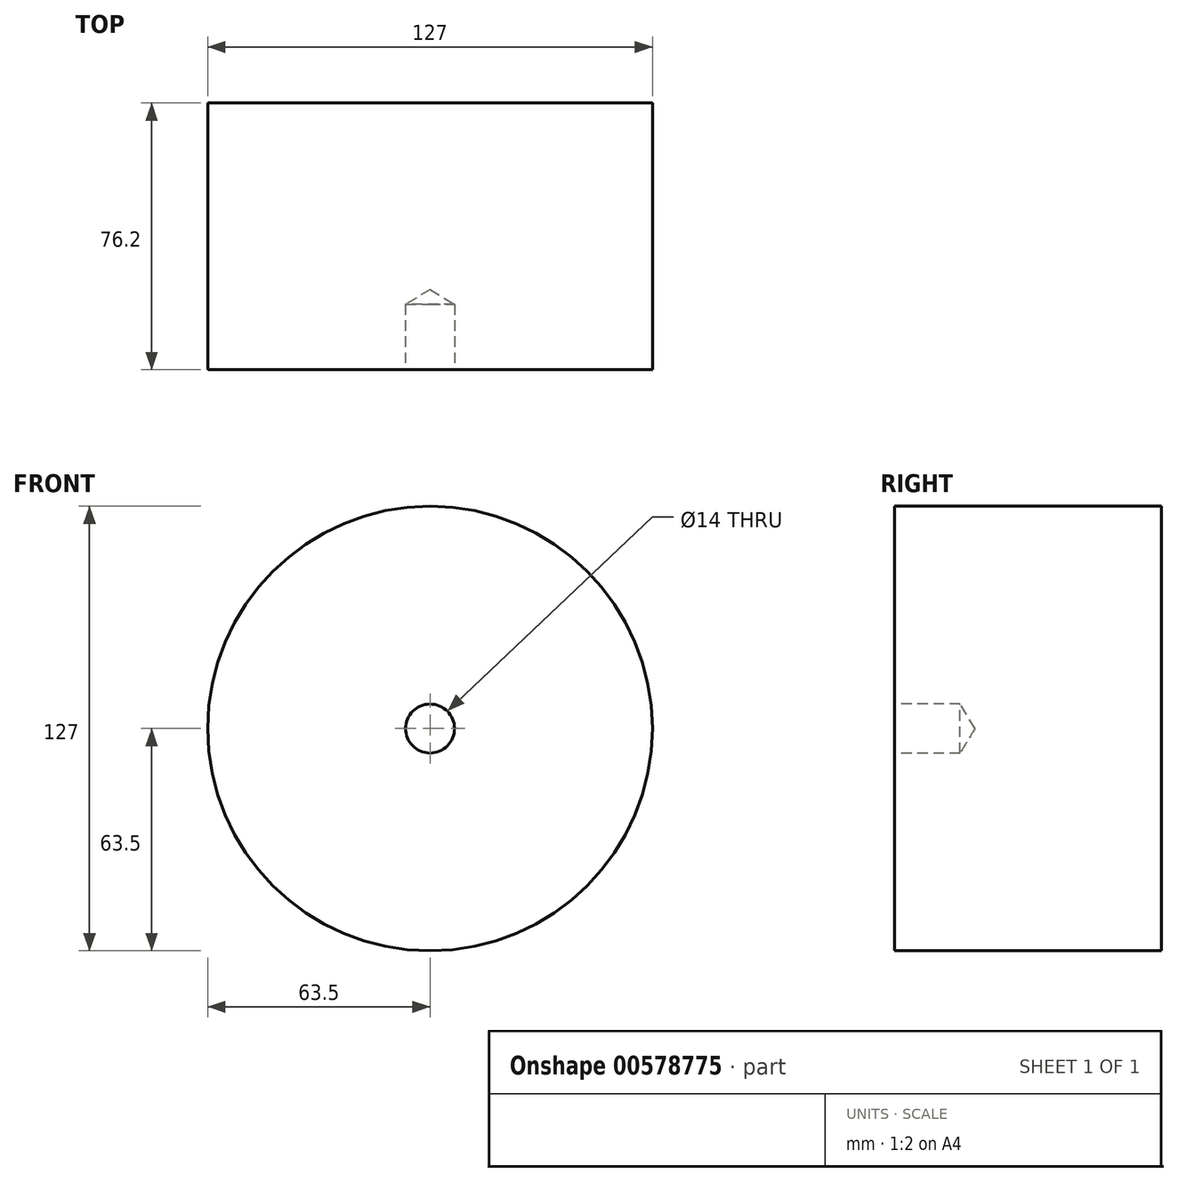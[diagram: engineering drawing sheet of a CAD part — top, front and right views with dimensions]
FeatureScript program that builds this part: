
annotation { "Feature Type Name" : "Feature", "Feature Type Description" : "" }
export const myFeature = defineFeature(function(context is Context, id is Id, definition is map)
    precondition{}
    {
        {
            var Q0;
            Q0=qCreatedBy(makeId("Front.planeOp"),FACE);
            var sketch = newSketch(context, id + "F0", { "sketchPlane" : qUnion([Q0])});
            skCircle(sketch, "E0", {"center": v(0, 0) * mm, "radius": 63.5 * mm});
            skSolve(sketch);
        }
        {
            var Q0;
            Q0=makeQuery(id+"F0.imprint","IMPRINT",FACE,{"disambiguationData":[TD([[makeQuery(id+"F0.imprint","IMPRINT",EDGE,{"derivedFrom":sQuery(id+"F0.wireOp",EDGE,"E0")}),1.0]])]});
            extrude(context, id + "F1", {"entities" : qUnion([Q0]), "depth" : 76.2 * mm, "offsetDistance" : 25.4 * mm});
        }
        {
            var Q0;
            Q0=makeQuery(id+"F1.opExtrude","CAP_FACE",FACE,{"disambiguationData":[OSD([sQuery(id+"F0.wireOp",EDGE,"E0")])],"isStart":false});
            var sketch = newSketch(context, id + "F2", { "sketchPlane" : qUnion([Q0])});
            skPoint(sketch, "E1", {"position": v(0, 0) * mm});
            skSolve(sketch);
        }
        {
            var Q0;
            Q0=sQuery(id+"F2.wireOp",VERTEX,"E1");
            var Q1;
            Q1=makeQuery(id+"F1.opExtrude","SWEPT_BODY",BODY,{"disambiguationData":[OSD([sQuery(id+"F0.wireOp",EDGE,"E0")])]});
            hole(context, id + "F3", {"style" : HoleStyle.SIMPLE, "endStyle" : HoleEndStyle.BLIND, "standardTappedOrClearance" : lookupTablePath({ "standard" : "ISO", "engagement" : "75%", "pitch" : "2 mm", "size" : "M16", "type" : "Tapped" }), "standardBlindInLast" : lookupTablePath({ "standard" : "ISO", "engagement" : "75%", "pitch" : "2 mm", "size" : "M16", "type" : "Tapped" }), "holeDiameter" : 14 * mm, "showTappedDepth" : true, "holeDepth" : 18.7 * mm, "isTappedThrough" : true, "tappedDepth" : 12.7 * mm, "tapClearance" : 3, "startFromSketch" : true, "locations" : qUnion([Q0]), "scope" : qUnion([Q1]), "majorDiameter" : 16 * mm});
        }
    });
